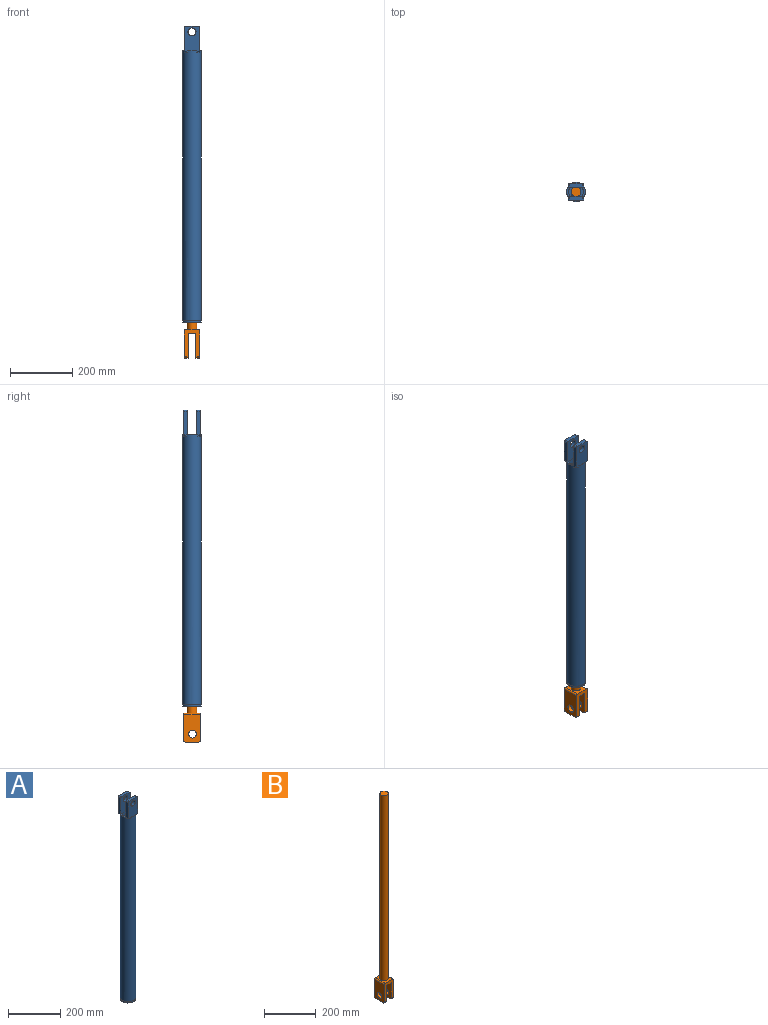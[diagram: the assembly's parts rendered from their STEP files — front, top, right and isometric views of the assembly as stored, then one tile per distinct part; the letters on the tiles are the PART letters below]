
ASSEMBLY  parts=2 mates=1
PART A: 37 faces, bbox 60.3x63.1x952.5 mm
  f0: plane 26.94x3.18mm, normal (0,0,1), area 57.7mm2, adj f5,f17
  f1: plane 32.53x11.11mm, normal (0,0,1), area 193.8mm2, adj f4,f5,f11,f12,f18,f19
  f2: plane 26.94x3.18mm, normal (0,0,1), area 57.7mm2, adj f5,f9
  f3: plane 32.53x11.11mm, normal (0,0,1), area 193.8mm2, adj f4,f5,f10,f11,f19,f20
  f4: cylinder r=23.81mm len=866.78mm, axis (0,0,-1), area 129685.4mm2, adj f1,f3,f14,f16,f33
  f5: cylinder r=30.16mm len=866.78mm, axis (0,0,-1), area 163938.4mm2, adj f0,f1,f2,f3,f6,f9,f10,f12
  f6: plane 60.33x60.33mm, normal (0,0,-1), area 76.7mm2, adj f5,f35
  f7: plane 2.74x2.56mm, normal (0,0,-1), area 3.4mm2, adj f9,f12,f29
  f8: plane 2.74x2.56mm, normal (0,0,-1), area 3.4mm2, adj f9,f10,f31
  f9: plane 84.46x50.8mm, normal (0,-1,0), area 3547.6mm2, adj f2,f5,f7,f8,f10,f12,f13,f23
  f10: plane 79.38x12.7mm, normal (1,0,0), area 965.1mm2, adj f3,f5,f8,f9,f11,f23,f31
  f11: plane 79.38x50.8mm, normal (0,1,0), area 3498.1mm2, adj f1,f3,f10,f12,f13,f14,f23,f24
  f12: plane 79.38x12.7mm, normal (-1,0,0), area 965.1mm2, adj f1,f5,f7,f9,f11,f24,f29
  f13: plane 40.64x12.7mm, normal (0,0,1), area 516.1mm2, adj f9,f11,f23,f24
  f14: plane 38.1x9.53mm, normal (0,0,-1), area 253.6mm2, adj f4,f11
  f15: plane 2.74x2.56mm, normal (0,0,-1), area 3.4mm2, adj f17,f20,f32
  f16: plane 38.1x9.53mm, normal (0,0,-1), area 253.6mm2, adj f4,f19
  f17: plane 84.46x50.8mm, normal (0,1,0), area 3547.6mm2, adj f0,f5,f15,f18,f20,f21,f22,f25
  f18: plane 79.38x12.7mm, normal (-1,0,0), area 965.1mm2, adj f1,f5,f17,f19,f22,f25,f30
  f19: plane 79.38x50.8mm, normal (0,-1,0), area 3498.1mm2, adj f1,f3,f16,f18,f20,f21,f25,f26
  f20: plane 79.38x12.7mm, normal (1,0,0), area 965.1mm2, adj f3,f5,f15,f17,f19,f26,f32
  f21: plane 40.64x12.7mm, normal (0,0,1), area 516.1mm2, adj f17,f19,f25,f26
  f22: plane 2.74x2.56mm, normal (0,0,-1), area 3.4mm2, adj f17,f18,f30
  f23: cylinder r=5.08mm len=12.7mm, axis (0,-1,0), area 101.3mm2, adj f9,f10,f11,f13
  f24: cylinder r=5.08mm len=12.7mm, axis (0,1,0), area 101.3mm2, adj f9,f11,f12,f13
  f25: cylinder r=5.08mm len=12.7mm, axis (0,1,0), area 101.3mm2, adj f17,f18,f19,f21
  f26: cylinder r=5.08mm len=12.7mm, axis (0,-1,0), area 101.3mm2, adj f17,f19,f20,f21
  f27: cylinder r=12.9mm len=25.81mm, axis (0,-1,0), area 1029.6mm2, adj f17,f19
  f28: cylinder r=12.9mm len=25.81mm, axis (0,-1,0), area 1029.6mm2, adj f9,f11
  f29: cone r=35.24mm half-angle=45deg, axis (0,0,1), area 69.2mm2, adj f5,f7,f9,f12
  f30: cone r=35.24mm half-angle=45deg, axis (0,0,1), area 69.2mm2, adj f5,f17,f18,f22
  f31: cone r=35.24mm half-angle=45deg, axis (0,0,1), area 69.2mm2, adj f5,f8,f9,f10
  f32: cone r=35.24mm half-angle=45deg, axis (0,0,1), area 69.2mm2, adj f5,f15,f17,f20
  f33: plane 47.63x47.63mm, normal (0,0,1), area 989.7mm2, adj f4,f34
  f34: cylinder r=15.88mm len=31.75mm, axis (0,0,1), area 633.4mm2, adj f33,f36
  f35: cylinder r=29.76mm len=59.51mm, axis (0,0,1), area 1187.2mm2, adj f6,f36
  f36: plane 59.51x59.51mm, normal (0,0,-1), area 1989.8mm2, adj f34,f35
PART B: 20 faces, bbox 50.8x54x968.4 mm
  f0: plane 43.82x12.7mm, normal (0,0,-1), area 556.5mm2, adj f2,f7,f16,f17
  f1: plane 87x50.8mm, normal (0,1,0), area 2521.2mm2, adj f2,f4,f5,f7,f8,f9,f15,f16
  f2: plane 87x53.98mm, normal (-1,0,0), area 4177.8mm2, adj f0,f1,f3,f11,f16,f17,f18
  f3: plane 87x50.8mm, normal (0,-1,0), area 2521.2mm2, adj f2,f4,f5,f7,f8,f9,f14,f17
  f4: plane 87x53.98mm, normal (1,0,0), area 4177.8mm2, adj f1,f3,f6,f10,f14,f15,f19
  f5: plane 53.98x40.64mm, normal (0,0,1), area 1401.8mm2, adj f1,f3,f12,f18,f19
  f6: plane 43.82x12.7mm, normal (0,0,-1), area 556.5mm2, adj f4,f8,f14,f15
  f7: plane 79.38x53.98mm, normal (1,0,0), area 3766.5mm2, adj f0,f1,f3,f9,f11,f16,f17
  f8: plane 79.38x53.98mm, normal (-1,0,0), area 3766.5mm2, adj f1,f3,f6,f9,f10,f14,f15
  f9: plane 53.98x25.4mm, normal (0,0,-1), area 1371mm2, adj f1,f3,f7,f8
  f10: cylinder r=12.7mm len=25.4mm, axis (1,0,0), area 1013.4mm2, adj f4,f8
  f11: cylinder r=12.7mm len=25.4mm, axis (1,0,0), area 1013.4mm2, adj f2,f7
  f12: cylinder r=15.88mm len=876.3mm, axis (0,0,-1), area 87407mm2, adj f5,f13
  f13: plane 31.75x31.75mm, normal (0,0,1), area 791.7mm2, adj f12
  f14: cylinder r=5.08mm len=12.7mm, axis (1,0,0), area 101.3mm2, adj f3,f4,f6,f8
  f15: cylinder r=5.08mm len=12.7mm, axis (-1,0,0), area 101.3mm2, adj f1,f4,f6,f8
  f16: cylinder r=5.08mm len=12.7mm, axis (-1,0,0), area 101.3mm2, adj f0,f1,f2,f7
  f17: cylinder r=5.08mm len=12.7mm, axis (1,0,0), area 101.3mm2, adj f0,f2,f3,f7
  f18: cylinder r=5.08mm len=53.98mm, axis (0,1,0), area 430.7mm2, adj f1,f2,f3,f5
  f19: cylinder r=5.08mm len=53.98mm, axis (0,-1,0), area 430.7mm2, adj f1,f3,f4,f5
PLACE A t=(-520.89,-72.82,-331.38)mm
PLACE B t=(-546.29,-99.81,-452.03)mm
MATE cylindrical B.f12 <-> A.f4  axis (0,0,1) through (-520.89,-72.82,516.34)mm
